# Revit family: Haworth_Planes_TrainingTable_Trapezoid
name_source: partatom
category: Furniture Systems
revit_build: Autodesk Revit 2018 (Build: 20170223_1515(x64)
units: mm (PartAtom-declared; Revit-internal decimal feet)

## family parameters
Always vertical = Yes
Cut with Voids When Loaded = No
OmniClass Number = 23.40.70.14.64.21
OmniClass Title = Systems Furniture
Part Type = Normal
Room Calculation Point = No
Round Connector Dimension = Use Diameter
Shared = No
Work Plane-Based = No

## types (1)
- 60w 30d
    Actual Depth = 30"
    Actual Height = 29"
    Actual Width = 60"
    Assembly Code = E2020200
    Casters = Yes
    Cutout = Yes
    Cutout Depth = 4"
    Cutout Width = 8"
    Description = Haworth - Planes Training - Table Trapezoid
    Edgeband = Yes
    Flip Top = Yes
    Flip Top Finish = Haworth _ Paint _ Metallic Champagne
    Fliptop Depth = 4 3/8"
    Fliptop Width = 8 1/4"
    Glides = No
    Knife Edge = No
    Leg Height = 27 13/16"
    Leg Placement = 26"
    Manufacturer = Haworth
    Model = TATP
    Opening Single = Yes
    Opening Single Narrow = No
    Opening Single Wide = No
    Revision Number = 3
    Size = Verify Final Dim. w/ Haworth
    Support Spacing - From Edge = 7 3/16"
    Sustainability Info = http://media.haworth.com
    Table Thickness = 1 3/16"
    URL = www.haworth.com
    URL - Product = http://www.haworth.com
    Void Cutout Height = 5"
    Void Height = 1 1/2"
    Void Top Placement = 31"
    Warranty = http://www.haworth.com

## geometry (parser evidence)
native form markers: Sweep x13
no freeform markers — native parametric forms only
